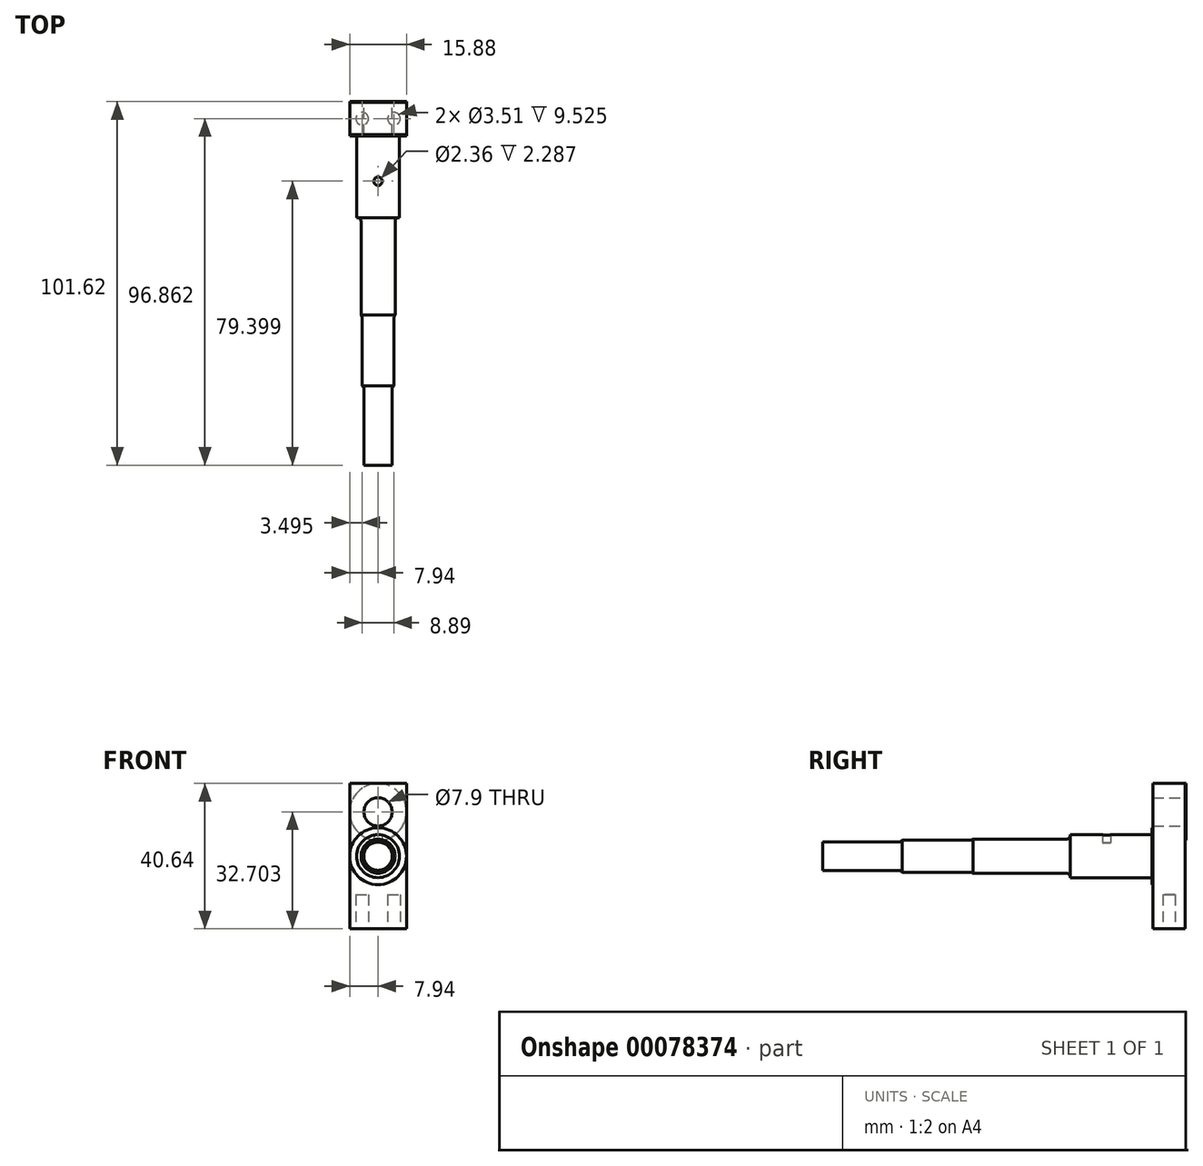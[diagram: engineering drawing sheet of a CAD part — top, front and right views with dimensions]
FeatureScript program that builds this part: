
annotation { "Feature Type Name" : "Feature", "Feature Type Description" : "" }
export const myFeature = defineFeature(function(context is Context, id is Id, definition is map)
    precondition{}
    {
        {
            var Q0;
            Q0=qCreatedBy(makeId("Front.planeOp"),FACE);
            var sketch = newSketch(context, id + "F0", { "sketchPlane" : qUnion([Q0])});
            skLineSegment(sketch, "E0.top", {"start": v(0, 20.32) * mm, "end": v(-7.94, 20.32) * mm});
            skLineSegment(sketch, "E0.right", {"start": v(-7.94, 0) * mm, "end": v(-7.94, 20.32) * mm});
            skLineSegment(sketch, "E1.MirrorCS", {"start": v(0, 20.32) * mm, "end": v(7.94, 20.32) * mm});
            skLineSegment(sketch, "E2.MirrorCS", {"start": v(7.94, 0) * mm, "end": v(7.94, 20.32) * mm});
            skLineSegment(sketch, "E3.MirrorCS", {"start": v(-7.94, 0) * mm, "end": v(-7.94, -20.32) * mm});
            skLineSegment(sketch, "E4.MirrorCS", {"start": v(0, -20.32) * mm, "end": v(-7.94, -20.32) * mm});
            skLineSegment(sketch, "E5.MirrorCS", {"start": v(0, -20.32) * mm, "end": v(7.94, -20.32) * mm});
            skLineSegment(sketch, "E6.MirrorCS", {"start": v(7.94, 0) * mm, "end": v(7.94, -20.32) * mm});
            skSolve(sketch);
        }
        {
            var Q0;
            Q0 = qSketchRegion(id + "F0", true);
            extrude(context, id + "F1", {"entities" : qUnion([Q0]), "depth" : 9.02 * mm});
        }
        {
            var Q0;
            Q0=makeQuery(id+"F1.opExtrude","CAP_FACE",FACE,{"disambiguationData":[OSD([sQuery(id+"F0.wireOp",EDGE,"E0.top"),sQuery(id+"F0.wireOp",EDGE,"E0.right"),sQuery(id+"F0.wireOp",EDGE,"E1.MirrorCS"),sQuery(id+"F0.wireOp",EDGE,"E2.MirrorCS"),sQuery(id+"F0.wireOp",EDGE,"E3.MirrorCS"),sQuery(id+"F0.wireOp",EDGE,"E4.MirrorCS"),sQuery(id+"F0.wireOp",EDGE,"E5.MirrorCS"),sQuery(id+"F0.wireOp",EDGE,"E6.MirrorCS")])],"isStart":false});
            var sketch = newSketch(context, id + "F2", { "sketchPlane" : qUnion([Q0])});
            skCircle(sketch, "E7", {"center": v(0, 0) * mm, "radius": 7.94 * mm});
            skSolve(sketch);
        }
        {
            var Q0;
            Q0 = qSketchRegion(id + "F2", true);
            extrude(context, id + "F3", {"entities" : qUnion([Q0]), "operationType" : NewBodyOperationType.ADD, "depth" : 0.28 * mm});
        }
        {
            var Q0;
            Q0=makeQuery(id+"F3.opExtrude","CAP_FACE",FACE,{"disambiguationData":[OSD([sQuery(id+"F2.wireOp",EDGE,"E7")])],"isStart":false});
            var sketch = newSketch(context, id + "F4", { "sketchPlane" : qUnion([Q0])});
            skCircle(sketch, "E8", {"center": v(0, 0) * mm, "radius": 6 * mm});
            skSolve(sketch);
        }
        {
            var Q0;
            Q0 = qSketchRegion(id + "F4", true);
            extrude(context, id + "F5", {"entities" : qUnion([Q0]), "operationType" : NewBodyOperationType.ADD, "depth" : 22.86 * mm});
        }
        {
            var Q0;
            Q0=makeQuery(id+"F3.opExtrude","CAP_FACE",FACE,{"disambiguationData":[OSD([sQuery(id+"F2.wireOp",EDGE,"E7")])],"isStart":false});
            var sketch = newSketch(context, id + "F6", { "sketchPlane" : qUnion([Q0])});
            skCircle(sketch, "E9", {"center": v(0, 0) * mm, "radius": 4.76 * mm});
            skSolve(sketch);
        }
        {
            var Q0;
            Q0 = qSketchRegion(id + "F6", true);
            extrude(context, id + "F7", {"entities" : qUnion([Q0]), "operationType" : NewBodyOperationType.ADD, "depth" : 50.06 * mm});
        }
        {
            var Q0;
            Q0=makeQuery(id+"F3.opExtrude","CAP_FACE",FACE,{"disambiguationData":[OSD([sQuery(id+"F2.wireOp",EDGE,"E7")])],"isStart":false});
            var sketch = newSketch(context, id + "F8", { "sketchPlane" : qUnion([Q0])});
            skCircle(sketch, "E10", {"center": v(0, 0) * mm, "radius": 4.5 * mm});
            skSolve(sketch);
        }
        {
            var Q0;
            Q0 = qSketchRegion(id + "F8", true);
            extrude(context, id + "F9", {"entities" : qUnion([Q0]), "operationType" : NewBodyOperationType.ADD, "depth" : 69.85 * mm});
        }
        {
            var Q0;
            Q0=makeQuery(id+"F3.opExtrude","CAP_FACE",FACE,{"disambiguationData":[OSD([sQuery(id+"F2.wireOp",EDGE,"E7")])],"isStart":false});
            var sketch = newSketch(context, id + "F10", { "sketchPlane" : qUnion([Q0])});
            skCircle(sketch, "E11", {"center": v(0, 0) * mm, "radius": 3.96 * mm});
            skSolve(sketch);
        }
        {
            var Q0;
            Q0 = qSketchRegion(id + "F10", true);
            extrude(context, id + "F11", {"entities" : qUnion([Q0]), "operationType" : NewBodyOperationType.ADD, "depth" : 92.07 * mm});
        }
        {
            var Q0;
            Q0=makeQuery(id+"F3.opExtrude","CAP_FACE",FACE,{"disambiguationData":[OSD([sQuery(id+"F2.wireOp",EDGE,"E7")])],"isStart":false});
            var sketch = newSketch(context, id + "F12", { "sketchPlane" : qUnion([Q0])});
            skCircle(sketch, "E12", {"center": v(0, 0) * mm, "radius": 3.97 * mm});
            skSolve(sketch);
        }
        {
            var Q0;
            Q0 = qSketchRegion(id + "F12", true);
            extrude(context, id + "F13", {"entities" : qUnion([Q0]), "operationType" : NewBodyOperationType.ADD, "depth" : 19.05 * mm});
        }
        {
            var Q0;
            Q0=makeQuery(id+"F7.boolean.opBoolean","INTERSECT",EDGE,{"derivedFrom":[makeQuery(id+"F5.opExtrude","CAP_FACE",FACE,{"disambiguationData":[OSD([sQuery(id+"F4.wireOp",EDGE,"E8")])],"isStart":false}),makeQuery(id+"F7.opExtrude","SWEPT_FACE",FACE,{"disambiguationData":[OSD([sQuery(id+"F6.wireOp",EDGE,"E9")])]})]});
            var Q1;
            Q1=makeQuery(id+"F9.boolean.opBoolean","INTERSECT",EDGE,{"derivedFrom":[makeQuery(id+"F7.opExtrude","CAP_FACE",FACE,{"disambiguationData":[OSD([sQuery(id+"F6.wireOp",EDGE,"E9")])],"isStart":false}),makeQuery(id+"F9.opExtrude","SWEPT_FACE",FACE,{"disambiguationData":[OSD([sQuery(id+"F8.wireOp",EDGE,"E10")])]})]});
            var Q2;
            Q2=makeQuery(id+"F11.boolean.opBoolean","INTERSECT",EDGE,{"derivedFrom":[makeQuery(id+"F9.opExtrude","CAP_FACE",FACE,{"disambiguationData":[OSD([sQuery(id+"F8.wireOp",EDGE,"E10")])],"isStart":false}),makeQuery(id+"F11.opExtrude","SWEPT_FACE",FACE,{"disambiguationData":[OSD([sQuery(id+"F10.wireOp",EDGE,"E11")])]})]});
            fillet(context, id + "F14", {"entities" : qUnion([Q0, Q1, Q2]), "radius" : 1.02 * mm, "tangentPropagation" : true, "allowEdgeOverflow" : false});
        }
        {
            var Q0;
            Q0=qCreatedBy(makeId("Right.planeOp"),FACE);
            var sketch = newSketch(context, id + "F15", { "sketchPlane" : qUnion([Q0])});
            skLineSegment(sketch, "E13", {"start": v(-21.97, 6) * mm, "end": v(-21.97, 3.71) * mm});
            skLineSegment(sketch, "E14", {"start": v(-21.97, 3.71) * mm, "end": v(-20.79, 3.71) * mm});
            skLineSegment(sketch, "E15", {"start": v(-20.79, 3.71) * mm, "end": v(-20.79, 6) * mm});
            skLineSegment(sketch, "E16", {"start": v(-21.97, 6) * mm, "end": v(-20.79, 6) * mm});
            skSolve(sketch);
        }
        {
            var Q0;
            Q0 = qSketchRegion(id + "F15", true);
            var Q1;
            Q1=sQuery(id+"F15.wireOp",EDGE,"E13");
            revolve(context, id + "F16", {"operationType" : NewBodyOperationType.REMOVE, "entities" : qUnion([Q0]), "axis" : qUnion([Q1]), "revolveType" : RevolveType.FULL, "oppositeDirection" : true});
        }
        {
            var Q0;
            Q0=makeQuery(id+"F1.opExtrude","CAP_FACE",FACE,{"disambiguationData":[OSD([sQuery(id+"F0.wireOp",EDGE,"E0.top"),sQuery(id+"F0.wireOp",EDGE,"E0.right"),sQuery(id+"F0.wireOp",EDGE,"E1.MirrorCS"),sQuery(id+"F0.wireOp",EDGE,"E2.MirrorCS"),sQuery(id+"F0.wireOp",EDGE,"E3.MirrorCS"),sQuery(id+"F0.wireOp",EDGE,"E4.MirrorCS"),sQuery(id+"F0.wireOp",EDGE,"E5.MirrorCS"),sQuery(id+"F0.wireOp",EDGE,"E6.MirrorCS")])],"isStart":true});
            var sketch = newSketch(context, id + "F17", { "sketchPlane" : qUnion([Q0])});
            skPoint(sketch, "E17.endSnap0", {"position": v(0, 20.32) * mm});
            skCircle(sketch, "E18", {"center": v(0, 12.38) * mm, "radius": 7.94 * mm});
            skSolve(sketch);
        }
        {
            var Q0;
            Q0 = qSketchRegion(id + "F17", true);
            extrude(context, id + "F18", {"entities" : qUnion([Q0]), "operationType" : NewBodyOperationType.ADD, "depth" : 0.25 * mm});
        }
        {
            var Q0;
            Q0=makeQuery(id+"F18.opExtrude","CAP_FACE",FACE,{"disambiguationData":[OSD([sQuery(id+"F17.wireOp",EDGE,"E18")])],"isStart":false});
            var sketch = newSketch(context, id + "F19", { "sketchPlane" : qUnion([Q0])});
            skLineSegment(sketch, "E19", {"start": v(0, 0) * mm, "end": v(0, 12.38) * mm, "construction": true});
            skCircle(sketch, "E20", {"center": v(0, 12.38) * mm, "radius": 3.95 * mm});
            skSolve(sketch);
        }
        {
            var Q0;
            Q0=makeQuery(id+"F19.imprint","IMPRINT",FACE,{"disambiguationData":[TD([[makeQuery(id+"F19.imprint","IMPRINT",EDGE,{"derivedFrom":sQuery(id+"F19.wireOp",EDGE,"E20")}),1.0]])]});
            extrude(context, id + "F20", {"entities" : qUnion([Q0]), "operationType" : NewBodyOperationType.REMOVE, "oppositeDirection" : true, "depth" : 25.4 * mm});
        }
        {
            var Q0;
            Q0=makeQuery(id+"F1.opExtrude","SWEPT_FACE",FACE,{"disambiguationData":[OSD([sQuery(id+"F0.wireOp",EDGE,"E4.MirrorCS"),sQuery(id+"F0.wireOp",EDGE,"E5.MirrorCS")])]});
            var sketch = newSketch(context, id + "F21", { "sketchPlane" : qUnion([Q0])});
            skLineSegment(sketch, "E21", {"start": v(0, 0) * mm, "end": v(0, 4.5) * mm, "construction": true});
            skLineSegment(sketch, "E22", {"start": v(0, 4.5) * mm, "end": v(4.45, 4.5) * mm, "construction": true});
            skCircle(sketch, "E23", {"center": v(4.45, 4.5) * mm, "radius": 1.75 * mm});
            skCircle(sketch, "E24.MirrorC", {"center": v(-4.44, 4.5) * mm, "radius": 1.75 * mm});
            skSolve(sketch);
        }
        {
            var Q0;
            Q0 = qSketchRegion(id + "F21", true);
            extrude(context, id + "F22", {"entities" : qUnion([Q0]), "operationType" : NewBodyOperationType.REMOVE, "oppositeDirection" : true, "depth" : 9.52 * mm});
        }
    });
